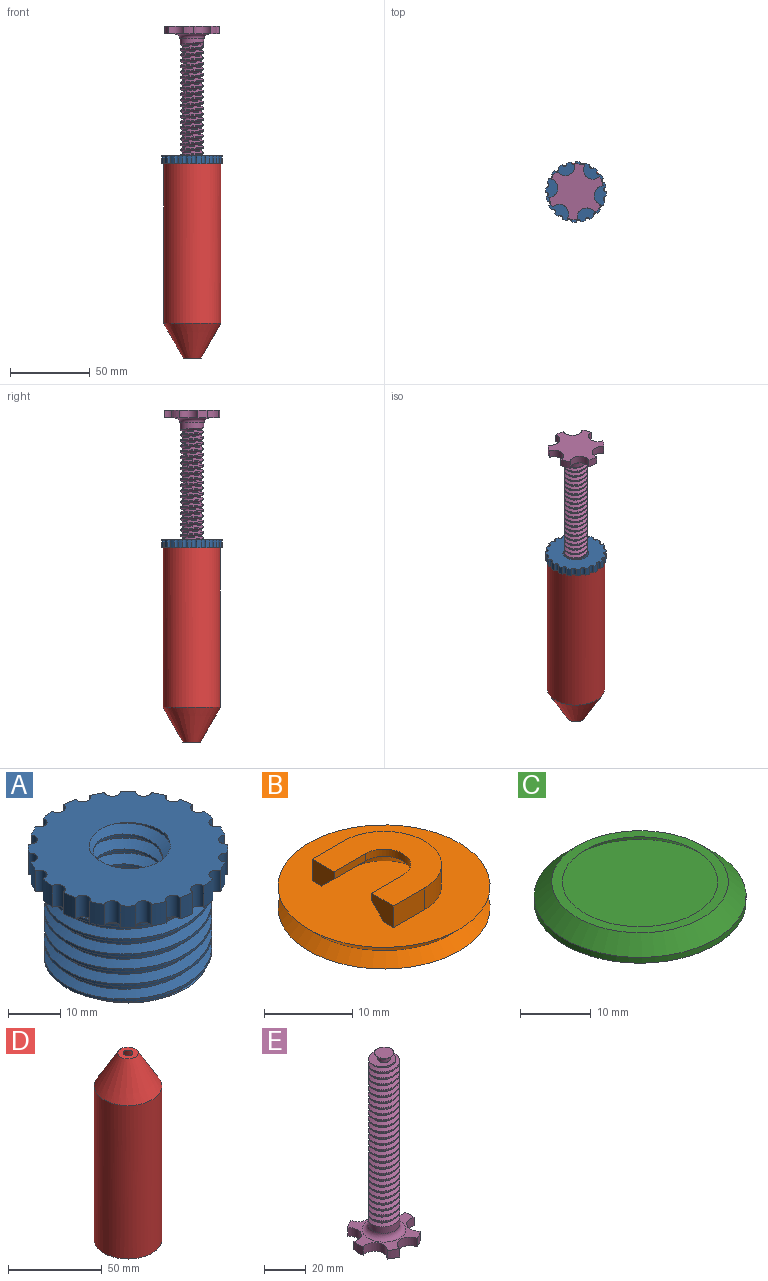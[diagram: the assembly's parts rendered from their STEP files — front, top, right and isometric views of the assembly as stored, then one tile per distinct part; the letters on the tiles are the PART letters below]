
ASSEMBLY  parts=5 mates=8
PART A: 53 faces, bbox 39x39x29.7 mm
  f0: cylinder r=19mm len=5mm, axis (0,0,-1), area 14.8mm2, adj f1,f3,f41,f42
  f1: cylinder r=1.5mm len=5mm, axis (0,0,1), area 23mm2, adj f0,f40,f41,f42
  f2: cylinder r=19mm len=5mm, axis (0,0,-1), area 14.8mm2, adj f3,f5,f41,f42
  f3: cylinder r=1.5mm len=5mm, axis (0,0,1), area 23mm2, adj f0,f2,f41,f42
  f4: cylinder r=19mm len=5mm, axis (0,0,-1), area 14.8mm2, adj f5,f7,f41,f42
  f5: cylinder r=1.5mm len=5mm, axis (0,0,1), area 23mm2, adj f2,f4,f41,f42
  f6: cylinder r=19mm len=5mm, axis (0,0,-1), area 14.8mm2, adj f7,f9,f41,f42
  f7: cylinder r=1.5mm len=5mm, axis (0,0,1), area 23mm2, adj f4,f6,f41,f42
  f8: cylinder r=19mm len=5mm, axis (0,0,-1), area 14.8mm2, adj f9,f11,f41,f42
  f9: cylinder r=1.5mm len=5mm, axis (0,0,1), area 23mm2, adj f6,f8,f41,f42
  f10: cylinder r=19mm len=5mm, axis (0,0,-1), area 14.8mm2, adj f11,f13,f41,f42
  f11: cylinder r=1.5mm len=5mm, axis (0,0,1), area 23mm2, adj f8,f10,f41,f42
  f12: cylinder r=19mm len=5mm, axis (0,0,-1), area 14.8mm2, adj f13,f15,f41,f42
  f13: cylinder r=1.5mm len=5mm, axis (0,0,1), area 23mm2, adj f10,f12,f41,f42
  f14: cylinder r=19mm len=5mm, axis (0,0,-1), area 14.8mm2, adj f15,f17,f41,f42
  f15: cylinder r=1.5mm len=5mm, axis (0,0,1), area 23mm2, adj f12,f14,f41,f42
  f16: cylinder r=19mm len=5mm, axis (0,0,-1), area 14.8mm2, adj f17,f19,f41,f42
  f17: cylinder r=1.5mm len=5mm, axis (0,0,1), area 23mm2, adj f14,f16,f41,f42
  f18: cylinder r=19mm len=5mm, axis (0,0,-1), area 14.8mm2, adj f19,f21,f41,f42
  f19: cylinder r=1.5mm len=5mm, axis (0,0,1), area 23mm2, adj f16,f18,f41,f42
  f20: cylinder r=19mm len=5mm, axis (0,0,-1), area 14.8mm2, adj f21,f23,f41,f42
  f21: cylinder r=1.5mm len=5mm, axis (0,0,1), area 23mm2, adj f18,f20,f41,f42
  f22: cylinder r=19mm len=5mm, axis (0,0,-1), area 14.8mm2, adj f23,f25,f41,f42
  f23: cylinder r=1.5mm len=5mm, axis (0,0,1), area 23mm2, adj f20,f22,f41,f42
  f24: cylinder r=19mm len=5mm, axis (0,0,-1), area 14.8mm2, adj f25,f27,f41,f42
  f25: cylinder r=1.5mm len=5mm, axis (0,0,1), area 23mm2, adj f22,f24,f41,f42
  f26: cylinder r=19mm len=5mm, axis (0,0,-1), area 14.8mm2, adj f27,f29,f41,f42
  f27: cylinder r=1.5mm len=5mm, axis (0,0,1), area 23mm2, adj f24,f26,f41,f42
  f28: cylinder r=19mm len=5mm, axis (0,0,-1), area 14.8mm2, adj f29,f31,f41,f42
  f29: cylinder r=1.5mm len=5mm, axis (0,0,1), area 23mm2, adj f26,f28,f41,f42
  f30: cylinder r=19mm len=5mm, axis (0,0,-1), area 14.8mm2, adj f31,f33,f41,f42
  f31: cylinder r=1.5mm len=5mm, axis (0,0,1), area 23mm2, adj f28,f30,f41,f42
  f32: cylinder r=19mm len=5mm, axis (0,0,-1), area 14.8mm2, adj f33,f35,f41,f42
  f33: cylinder r=1.5mm len=5mm, axis (0,0,1), area 23mm2, adj f30,f32,f41,f42
  f34: cylinder r=19mm len=5mm, axis (0,0,-1), area 14.8mm2, adj f35,f37,f41,f42
  f35: cylinder r=1.5mm len=5mm, axis (0,0,1), area 23mm2, adj f32,f34,f41,f42
  f36: cylinder r=19mm len=5mm, axis (0,0,-1), area 14.8mm2, adj f37,f41,f42,f48
  f37: cylinder r=1.5mm len=5mm, axis (0,0,1), area 23mm2, adj f34,f36,f41,f42
  f38: cylinder r=16mm len=32mm, axis (0,0,-1), area 361.7mm2, adj f39,f42,f44,f45
  f39: plane 31.31x31.17mm, normal (0,0,-1), area 527.8mm2, adj f38,f43,f44,f45,f49,f50,f51,f52
  f40: cylinder r=19mm len=5mm, axis (0,0,-1), area 14.8mm2, adj f1,f41,f42,f48
  f41: plane 38.96x38.96mm, normal (0,0,1), area 878.8mm2, adj f0,f1,f2,f3,f4,f5,f6,f7
  f42: plane 38.23x38.23mm, normal (0,0,-1), area 245.3mm2, adj f0,f1,f2,f3,f4,f5,f6,f7
  f43: cylinder r=14.25mm len=28.5mm, axis (0,0,-1), area 673.3mm2, adj f39,f44,f45,f47
  f44: bspline ~36.95x32mm, area 1281.8mm2, adj f38,f39,f43,f46,f47
  f45: bspline ~36.95x32mm, area 1190.5mm2, adj f38,f39,f43,f47
  f46: bspline ~37.79x32.73mm, area 124.9mm2, adj f42,f44,f47
  f47: plane 2.91x2.03mm, normal (0,-1,0), area 3.8mm2, adj f43,f44,f45,f46
  f48: cylinder r=1.5mm len=5mm, axis (0,0,1), area 23mm2, adj f36,f40,f41,f42
  f49: cylinder r=6.6mm len=26mm, axis (0,0,1), area 131.5mm2, adj f39,f41,f51,f52
  f50: cylinder r=8.6mm len=26mm, axis (0,0,-1), area 324.5mm2, adj f39,f41,f51,f52
  f51: bspline ~28.57x19.86mm, area 820.9mm2, adj f39,f41,f49,f50
  f52: bspline ~28.57x19.86mm, area 820.6mm2, adj f39,f41,f49,f50
PART B: 16 faces, bbox 24x24x6 mm
  f0: plane 24x24mm, normal (0,0,1), area 410.3mm2, adj f1,f2,f5,f7,f8,f9,f10,f12
  f1: cylinder r=6.5mm len=13mm, axis (0,0,-1), area 61.3mm2, adj f0,f4,f5,f9
  f2: cone r=5mm half-angle=45deg, axis (0,0,-1), area 35.5mm2, adj f0,f3,f7,f10
  f3: cylinder r=3mm len=6mm, axis (0,0,-1), area 9.4mm2, adj f2,f4,f6,f11
  f4: plane 13x11.5mm, normal (0,0,1), area 87.2mm2, adj f1,f3,f5,f6,f8,f9,f11,f12
  f5: plane 5x3mm, normal (0,-1,0), area 15mm2, adj f0,f1,f4,f8
  f6: plane 5x1mm, normal (0,1,0), area 5mm2, adj f3,f4,f7,f8
  f7: plane 5x2mm, normal (0,0.71,-0.71), area 14.1mm2, adj f0,f2,f6,f8
  f8: plane 3.5x3mm, normal (-1,0,0), area 8.5mm2, adj f0,f4,f5,f6,f7
  f9: plane 5x3mm, normal (0,1,0), area 15mm2, adj f0,f1,f4,f12
  f10: plane 5x2mm, normal (0,-0.71,-0.71), area 14.1mm2, adj f0,f2,f11,f12
  f11: plane 5x1mm, normal (0,-1,0), area 5mm2, adj f3,f4,f10,f12
  f12: plane 3.5x3mm, normal (-1,0,0), area 8.5mm2, adj f0,f4,f9,f10,f11
  f13: cone r=12mm half-angle=45deg, axis (0,0,-1), area 149.9mm2, adj f14,f15
  f14: cone r=10.5mm half-angle=45deg, axis (0,0,1), area 149.9mm2, adj f0,f13
  f15: plane 24x24mm, normal (0,0,-1), area 452.4mm2, adj f13
PART C: 6 faces, bbox 30x30x3.5 mm
  f0: cone r=11mm half-angle=45deg, axis (0,0,-1), area 156.6mm2, adj f1,f5
  f1: plane 25x25mm, normal (0,0,1), area 110.7mm2, adj f0,f2
  f2: cone r=15mm half-angle=45deg, axis (0,0,-1), area 305.4mm2, adj f1,f3
  f3: cylinder r=15mm len=30mm, axis (0,0,1), area 94.2mm2, adj f2,f4
  f4: plane 30x30mm, normal (0,0,-1), area 706.9mm2, adj f3
  f5: plane 25x25mm, normal (0,0,1), area 490.9mm2, adj f0
PART D: 15 faces, bbox 40.5x37.2x124.1 mm
  f0: cylinder r=15mm len=26.64mm, axis (0,0,-1), area 15.1mm2, adj f1,f7,f8,f10
  f1: cylinder r=15mm len=30mm, axis (0,0,-1), area 47.1mm2, adj f0,f2,f8,f10
  f2: cylinder r=15mm len=30mm, axis (0,0,-1), area 47.1mm2, adj f1,f3,f8,f10
  f3: cylinder r=15mm len=30mm, axis (0,0,-1), area 47.1mm2, adj f2,f4,f8,f10
  f4: cylinder r=15mm len=30mm, axis (0,0,-1), area 47.1mm2, adj f3,f5,f8,f10
  f5: cylinder r=15mm len=85.13mm, axis (0,0,-1), area 7645.8mm2, adj f4,f8,f10,f11,f14
  f6: cylinder r=18mm len=100mm, axis (0,0,-1), area 11309.7mm2, adj f7,f12
  f7: plane 37.21x37.21mm, normal (0,0,-1), area 206.4mm2, adj f0,f6,f8,f9,f10
  f8: bspline ~39.26x34mm, area 1353.3mm2, adj f0,f1,f2,f3,f4,f5,f7,f9
  f9: cylinder r=17mm len=34mm, axis (0,0,1), area 396.4mm2, adj f7,f8,f10,f11
  f10: bspline ~39.26x34mm, area 1233.3mm2, adj f0,f1,f2,f3,f4,f5,f7,f9
  f11: plane 3x2mm, normal (1,0,0), area 3.7mm2, adj f5,f8,f9,f10
  f12: cone r=18mm half-angle=30deg, axis (0,0,-1), area 1845.7mm2, adj f6,f13
  f13: plane 11x11mm, normal (0,0,1), area 75.4mm2, adj f12,f14
  f14: cone r=2.5mm half-angle=30deg, axis (0,0,-1), area 1374.4mm2, adj f5,f13
PART E: 50 faces, bbox 35.9x33.8x109.6 mm
  f0: plane 14.06x14.03mm, normal (0,0,1), area 107.8mm2, adj f13,f44,f45,f46,f47
  f1: cylinder r=17.5mm len=5.4mm, axis (0,0,1), area 31.3mm2, adj f2,f11,f40,f42
  f2: cylinder r=6mm len=10.61mm, axis (0,0,1), area 83.9mm2, adj f1,f3,f11,f40
  f3: cylinder r=17.5mm len=6.23mm, axis (0,0,1), area 31.3mm2, adj f2,f4,f11,f40
  f4: cylinder r=6mm len=10.61mm, axis (0,0,1), area 83.9mm2, adj f3,f5,f11,f40
  f5: cylinder r=17.5mm len=5.4mm, axis (0,0,1), area 31.3mm2, adj f4,f6,f11,f40
  f6: cylinder r=6mm len=11.82mm, axis (0,0,1), area 83.9mm2, adj f5,f7,f11,f40
  f7: cylinder r=17.5mm len=5.4mm, axis (0,0,1), area 31.3mm2, adj f6,f8,f11,f40
  f8: cylinder r=6mm len=10.61mm, axis (0,0,1), area 83.9mm2, adj f7,f9,f11,f40
  f9: cylinder r=17.5mm len=6.23mm, axis (0,0,1), area 31.3mm2, adj f8,f10,f11,f40
  f10: cylinder r=6mm len=10.61mm, axis (0,0,1), area 83.9mm2, adj f9,f11,f39,f40
  f11: plane 35x32.94mm, normal (0,0,1), area 301.2mm2, adj f1,f2,f3,f4,f5,f6,f7,f8
  f12: cylinder r=7.5mm len=15mm, axis (0,0,-1), area 187.8mm2, adj f38,f41,f43,f44,f45
  f13: cylinder r=7.5mm len=15mm, axis (0,0,-1), area 23.7mm2, adj f0,f14,f44,f45
  f14: cylinder r=7.5mm len=15mm, axis (0,0,-1), area 28.3mm2, adj f13,f15,f44,f45
  f15: cylinder r=7.5mm len=15mm, axis (0,0,-1), area 28.3mm2, adj f14,f16,f44,f45
  f16: cylinder r=7.5mm len=15mm, axis (0,0,-1), area 28.3mm2, adj f15,f17,f44,f45
  f17: cylinder r=7.5mm len=15mm, axis (0,0,-1), area 28.3mm2, adj f16,f18,f44,f45
  f18: cylinder r=7.5mm len=15mm, axis (0,0,-1), area 28.3mm2, adj f17,f19,f44,f45
  f19: cylinder r=7.5mm len=15mm, axis (0,0,-1), area 28.3mm2, adj f18,f20,f44,f45
  f20: cylinder r=7.5mm len=15mm, axis (0,0,-1), area 28.3mm2, adj f19,f21,f44,f45
  f21: cylinder r=7.5mm len=15mm, axis (0,0,-1), area 28.3mm2, adj f20,f22,f44,f45
  f22: cylinder r=7.5mm len=15mm, axis (0,0,-1), area 28.3mm2, adj f21,f23,f44,f45
  f23: cylinder r=7.5mm len=15mm, axis (0,0,-1), area 28.3mm2, adj f22,f24,f44,f45
  f24: cylinder r=7.5mm len=15mm, axis (0,0,-1), area 28.3mm2, adj f23,f25,f44,f45
  f25: cylinder r=7.5mm len=15mm, axis (0,0,-1), area 28.3mm2, adj f24,f26,f44,f45
  f26: cylinder r=7.5mm len=15mm, axis (0,0,-1), area 28.3mm2, adj f25,f27,f44,f45
  f27: cylinder r=7.5mm len=15mm, axis (0,0,-1), area 28.3mm2, adj f26,f28,f44,f45
  f28: cylinder r=7.5mm len=15mm, axis (0,0,-1), area 28.3mm2, adj f27,f29,f44,f45
  f29: cylinder r=7.5mm len=15mm, axis (0,0,-1), area 28.3mm2, adj f28,f30,f44,f45
  f30: cylinder r=7.5mm len=15mm, axis (0,0,-1), area 28.3mm2, adj f29,f31,f44,f45
  f31: cylinder r=7.5mm len=15mm, axis (0,0,-1), area 28.3mm2, adj f30,f32,f44,f45
  f32: cylinder r=7.5mm len=15mm, axis (0,0,-1), area 28.3mm2, adj f31,f33,f44,f45
  f33: cylinder r=7.5mm len=15mm, axis (0,0,-1), area 28.3mm2, adj f32,f34,f44,f45
  f34: cylinder r=7.5mm len=15mm, axis (0,0,-1), area 28.3mm2, adj f33,f35,f44,f45
  f35: cylinder r=7.5mm len=15mm, axis (0,0,-1), area 28.3mm2, adj f34,f36,f44,f45
  f36: cylinder r=7.5mm len=15mm, axis (0,0,-1), area 28.3mm2, adj f35,f37,f44,f45
  f37: cylinder r=7.5mm len=15mm, axis (0,0,-1), area 28.3mm2, adj f36,f38,f44,f45
  f38: cylinder r=7.5mm len=15mm, axis (0,0,-1), area 28.3mm2, adj f12,f37,f44,f45
  f39: cylinder r=17.5mm len=5.4mm, axis (0,0,1), area 31.3mm2, adj f10,f11,f40,f42
  f40: plane 35x32.94mm, normal (0,0,-1), area 647.6mm2, adj f1,f2,f3,f4,f5,f6,f7,f8
  f41: torus R=10.5mm, axis (0,0,-1), area 254.3mm2, adj f11,f12
  f42: cylinder r=6mm len=11.82mm, axis (0,0,1), area 83.9mm2, adj f1,f11,f39,f40
  f43: plane 2.91x1.42mm, normal (-0.62,0.78,0), area 3.3mm2, adj f12,f44,f45,f46
  f44: bspline ~96.12x17.32mm, area 2333.9mm2, adj f0,f12,f13,f14,f15,f16,f17,f18
  f45: bspline ~94.37x17.32mm, area 2268.3mm2, adj f0,f12,f13,f14,f15,f16,f17,f18
  f46: cylinder r=5.7mm len=93.97mm, axis (0,0,-1), area 24.9mm2, adj f0,f43,f44,f45
  f47: cylinder r=3mm len=6mm, axis (0,0,-1), area 37.7mm2, adj f0,f48
  f48: cone r=3mm half-angle=45deg, axis (0,0,1), area 58.2mm2, adj f47,f49
  f49: plane 9.4x9.4mm, normal (0,0,1), area 69.4mm2, adj f48
PLACE A rot(axis=(0,0,-1),157.5deg) t=(71.48,-32.05,-70.91)mm
PLACE B t=(71.48,-32.05,-75.25)mm
PLACE C t=(71.48,-32.05,-77.25)mm
PLACE D rot(axis=(0.2,-0.98,0),180deg) t=(71.63,-31.88,-49.91)mm
PLACE E rot(axis=(0.98,0.2,0),180deg) t=(71.48,-32.05,31.45)mm
MATE planar A.f42 <-> D.f7  axis (0,0,-1) through (71.2,-32.42,-49.91)mm
MATE cylindrical C.f0 <-> B.f13  axis (0,0,-1) through (71.48,-32.05,-77.25)mm
MATE cylindrical B.f13 <-> E.f47  axis (0,0,1) through (71.48,-32.05,-72.25)mm
MATE planar C.f0 <-> B.f13  axis (0,0,1) through (71.48,-32.05,-75.25)mm
MATE planar E.f47 <-> B.f13  axis (0,0,-1) through (71.48,-32.05,-72.25)mm
MATE cylindrical A.f41 <-> D.f6  axis (0,0,1) through (71.63,-31.88,-44.91)mm
MATE cylindrical B.f13 <-> C.f0  axis (0,0,-1) through (71.48,-32.05,-75.25)mm
MATE cylindrical E.f1 <-> A.f0  axis (0,0,-1) through (71.48,-32.05,31.45)mm
